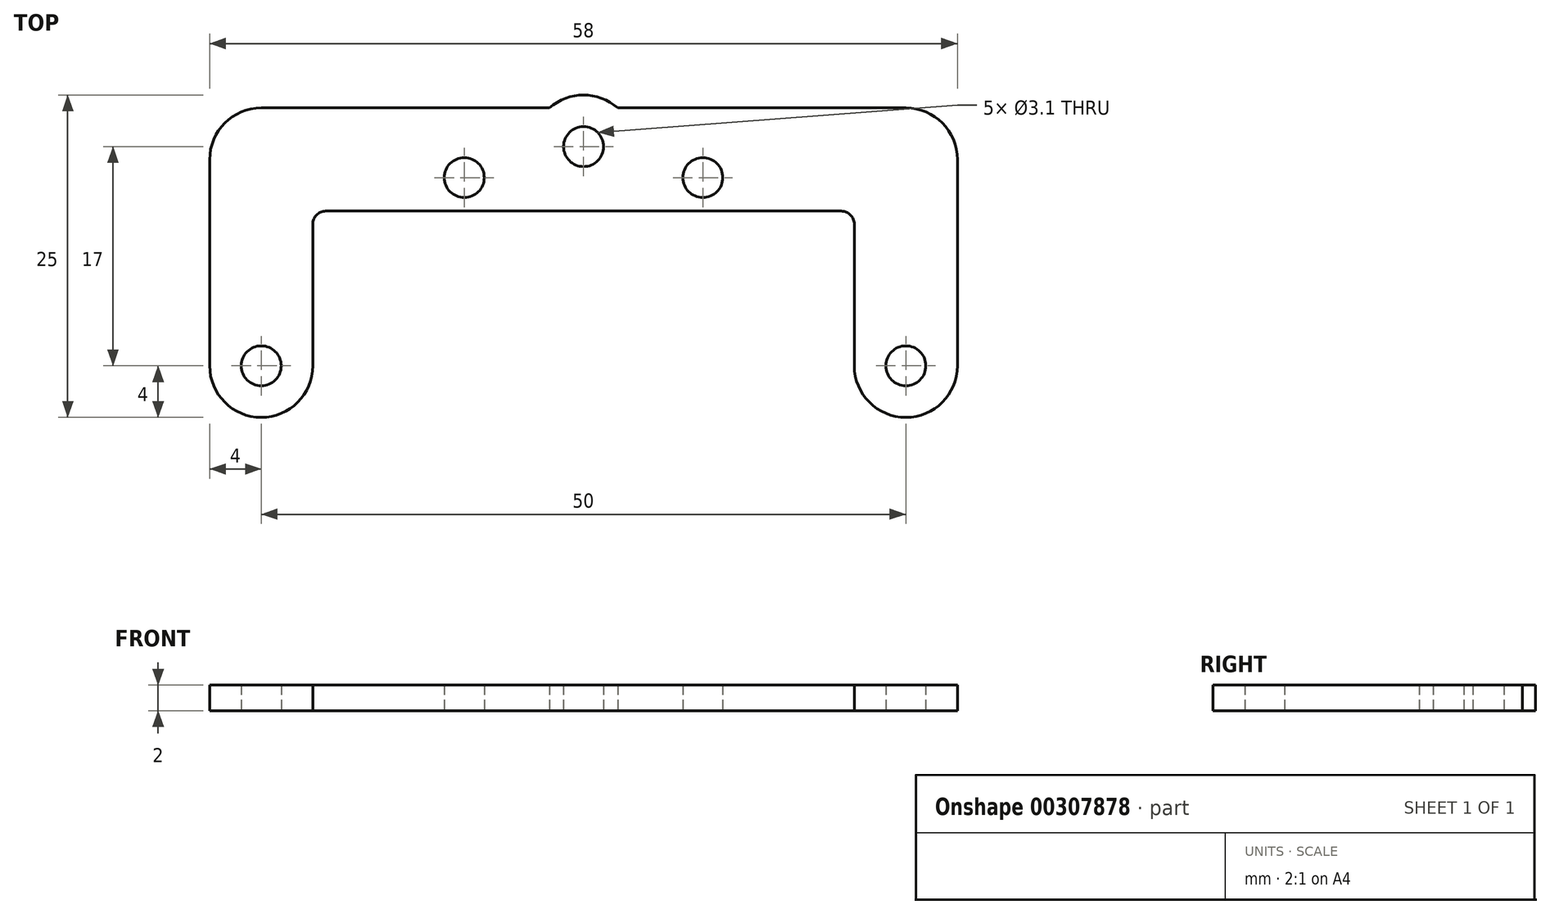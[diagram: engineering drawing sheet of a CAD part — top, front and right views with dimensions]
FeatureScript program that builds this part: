
annotation { "Feature Type Name" : "Feature", "Feature Type Description" : "" }
export const myFeature = defineFeature(function(context is Context, id is Id, definition is map)
    precondition{}
    {
        {
            var Q0;
            Q0=qCreatedBy(makeId("Top.planeOp"),FACE);
            var sketch = newSketch(context, id + "F0", { "sketchPlane" : qUnion([Q0])});
            skLineSegment(sketch, "E0.bottom", {"start": v(20, -5) * mm, "end": v(-20, -5) * mm});
            skPoint(sketch, "E0.middle", {"position": v(0, 0) * mm});
            skCircle(sketch, "E1", {"center": v(9.25, -2.4) * mm, "radius": 1.55 * mm});
            skCircle(sketch, "E2", {"center": v(-9.25, -2.4) * mm, "radius": 1.55 * mm});
            skCircle(sketch, "E3", {"center": v(0, 0) * mm, "radius": 1.55 * mm});
            skLineSegment(sketch, "E4.top", {"start": v(25, -21) * mm, "end": v(25, -21) * mm});
            skLineSegment(sketch, "E4.left", {"start": v(21, -6) * mm, "end": v(21, -17) * mm});
            skLineSegment(sketch, "E4.right", {"start": v(29, -1) * mm, "end": v(29, -17) * mm});
            skLineSegment(sketch, "E5.MirrorCS", {"start": v(-21, -6) * mm, "end": v(-21, -17) * mm});
            skLineSegment(sketch, "E6.MirrorCS", {"start": v(-25, -21) * mm, "end": v(-25, -21) * mm});
            skCircle(sketch, "E7", {"center": v(25, -17) * mm, "radius": 1.55 * mm});
            skCircle(sketch, "E8.MirrorC", {"center": v(-25, -17) * mm, "radius": 1.55 * mm});
            skPoint(sketch, "E9.newPointA", {"position": v(20, -5) * mm});
            skArc(sketch, "E9.filletArc", {"start": v(21, -6) * mm, "mid": v(20.7, -5.3) * mm, "end": v(20, -5) * mm});
            skPoint(sketch, "E10.newPointA", {"position": v(-20, -5) * mm});
            skArc(sketch, "E10.filletArc", {"start": v(-20, -5) * mm, "mid": v(-20.7, -5.3) * mm, "end": v(-21, -6) * mm});
            skPoint(sketch, "E11.visualSharp", {"position": v(-29, -21) * mm});
            skArc(sketch, "E11.filletArc", {"start": v(-29, -17) * mm, "mid": v(-27.83, -19.83) * mm, "end": v(-25, -21) * mm});
            skPoint(sketch, "E12.visualSharp", {"position": v(-21, -21) * mm});
            skArc(sketch, "E12.filletArc", {"start": v(-25, -21) * mm, "mid": v(-22.17, -19.83) * mm, "end": v(-21, -17) * mm});
            skPoint(sketch, "E13.visualSharp", {"position": v(21, -21) * mm});
            skArc(sketch, "E13.filletArc", {"start": v(21, -17) * mm, "mid": v(22.17, -19.83) * mm, "end": v(25, -21) * mm});
            skPoint(sketch, "E14.visualSharp", {"position": v(29, -21) * mm});
            skArc(sketch, "E14.filletArc", {"start": v(25, -21) * mm, "mid": v(27.83, -19.83) * mm, "end": v(29, -17) * mm});
            skPoint(sketch, "E15.visualSharp", {"position": v(29, 3) * mm});
            skLineSegment(sketch, "E16", {"start": v(25, 3) * mm, "end": v(2.65, 3) * mm});
            skArc(sketch, "E17", {"start": v(-2.65, 3) * mm, "mid": v(0, 4) * mm, "end": v(2.65, 3) * mm});
            skArc(sketch, "E18.filletArc", {"start": v(29, -1) * mm, "mid": v(27.83, 1.83) * mm, "end": v(25, 3) * mm});
            skLineSegment(sketch, "E19.MirrorCS", {"start": v(-25, 3) * mm, "end": v(-2.65, 3) * mm});
            skArc(sketch, "E20.MirrorCS", {"start": v(-29, -1) * mm, "mid": v(-27.83, 1.83) * mm, "end": v(-25, 3) * mm});
            skLineSegment(sketch, "E21.MirrorCS", {"start": v(-29, -1) * mm, "end": v(-29, -17) * mm});
            skPoint(sketch, "E22.MirrorP", {"position": v(-29, 3) * mm});
            skSolve(sketch);
        }
        {
            var Q0;
            Q0=makeQuery(id+"F0.imprint","IMPRINT",FACE,{"disambiguationData":[TD([[makeQuery(id+"F0.imprint","IMPRINT",EDGE,{"derivedFrom":sQuery(id+"F0.wireOp",EDGE,"E0.bottom")}),-1.0]])]});
            extrude(context, id + "F1", {"entities" : qUnion([Q0]), "depth" : 2 * mm});
        }
    });
